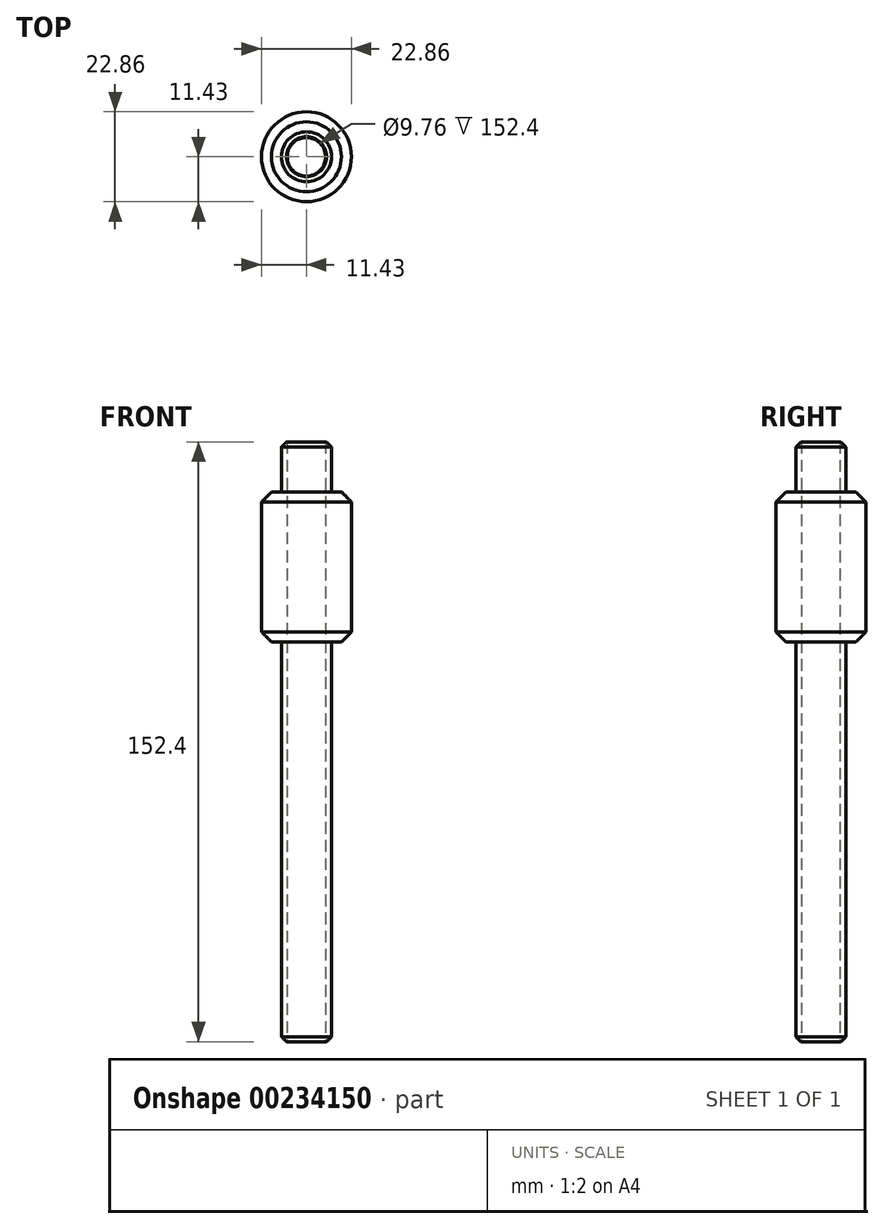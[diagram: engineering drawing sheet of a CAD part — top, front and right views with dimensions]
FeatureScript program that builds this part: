
annotation { "Feature Type Name" : "Feature", "Feature Type Description" : "" }
export const myFeature = defineFeature(function(context is Context, id is Id, definition is map)
    precondition{}
    {
        {
            var Q0;
            Q0=qCreatedBy(makeId("Front.planeOp"),FACE);
            var sketch = newSketch(context, id + "F0", { "sketchPlane" : qUnion([Q0])});
            skLineSegment(sketch, "E0.bottom", {"start": v(6.35, -76.2) * mm, "end": v(-6.35, -76.2) * mm});
            skLineSegment(sketch, "E0.top", {"start": v(6.35, 76.2) * mm, "end": v(-6.35, 76.2) * mm});
            skLineSegment(sketch, "E0.left", {"start": v(6.35, -76.2) * mm, "end": v(6.35, 25.4) * mm});
            skLineSegment(sketch, "E0.right", {"start": v(-6.35, -76.2) * mm, "end": v(-6.35, 76.2) * mm});
            skPoint(sketch, "E0.middle", {"position": v(0, 0) * mm});
            skLineSegment(sketch, "E1", {"start": v(6.35, 63.5) * mm, "end": v(11.43, 63.5) * mm});
            skLineSegment(sketch, "E2", {"start": v(11.43, 63.5) * mm, "end": v(11.43, 25.4) * mm});
            skLineSegment(sketch, "E3", {"start": v(11.43, 25.4) * mm, "end": v(6.35, 25.4) * mm});
            skLineSegment(sketch, "E4.trimOffspring", {"start": v(6.35, 63.5) * mm, "end": v(6.35, 76.2) * mm});
            skLineSegment(sketch, "E5", {"start": v(0, 89.32) * mm, "end": v(0, -93.51) * mm});
            skPoint(sketch, "E5.startSnap0", {"position": v(0, 76.2) * mm});
            skSolve(sketch);
        }
        {
            var Q0;
            {var subQ0=sQuery(id+"F0.wireOp",EDGE,"E0.left");Q0=makeQuery(id+"F0.imprint","IMPRINT",FACE,{"disambiguationData":[TD([[makeQuery(id+"F0.imprint","IMPRINT",EDGE,{"derivedFrom":subQ0}),1.0]])]});}
            var Q1;
            Q1=sQuery(id+"F0.wireOp",EDGE,"E5");
            revolve(context, id + "F1", {"entities" : qUnion([Q0]), "axis" : qUnion([Q1]), "revolveType" : RevolveType.FULL});
        }
        {
            var Q0;
            Q0=makeQuery(id+"F1.opRevolve","SWEPT_EDGE",EDGE,{"disambiguationData":[OSD([sQuery(id+"F0.wireOp",EDGE,"E2"),sQuery(id+"F0.wireOp",EDGE,"E3")])]});
            chamfer(context, id + "F2", {"entities" : qUnion([Q0]), "width" : 2.54 * mm, "tangentPropagation" : true});
        }
        {
            var Q0;
            Q0=makeQuery(id+"F1.opRevolve","SWEPT_FACE",FACE,{"disambiguationData":[OSD([sQuery(id+"F0.wireOp",EDGE,"E0.bottom")])]});
            var sketch = newSketch(context, id + "F3", { "sketchPlane" : qUnion([Q0])});
            skCircle(sketch, "E6", {"center": v(0, 0) * mm, "radius": 4.88 * mm});
            skSolve(sketch);
        }
        {
            var Q0;
            Q0=makeQuery(id+"F3.imprint","IMPRINT",FACE,{"disambiguationData":[TD([[makeQuery(id+"F3.imprint","IMPRINT",EDGE,{"derivedFrom":sQuery(id+"F3.wireOp",EDGE,"E6")}),1.0]])]});
            extrude(context, id + "F6", {"entities" : qUnion([Q0]), "operationType" : NewBodyOperationType.REMOVE, "endBound" : BoundingType.THROUGH_ALL, "oppositeDirection" : true, "depth" : 25.4 * mm});
        }
        {
            var Q0;
            Q0=makeQuery(id+"F1.opRevolve","SWEPT_EDGE",EDGE,{"disambiguationData":[OSD([sQuery(id+"F0.wireOp",EDGE,"E0.top"),sQuery(id+"F0.wireOp",EDGE,"E4.trimOffspring")])]});
            chamfer(context, id + "F4", {"entities" : qUnion([Q0]), "width" : 1.27 * mm, "tangentPropagation" : true});
        }
        {
            var Q0;
            Q0=makeQuery(id+"F1.opRevolve","SWEPT_EDGE",EDGE,{"disambiguationData":[OSD([sQuery(id+"F0.wireOp",EDGE,"E1"),sQuery(id+"F0.wireOp",EDGE,"E2")])]});
            chamfer(context, id + "F7", {"entities" : qUnion([Q0]), "width" : 2.54 * mm, "tangentPropagation" : true});
        }
        {
            var Q0;
            Q0=makeQuery(id+"F1.opRevolve","SWEPT_EDGE",EDGE,{"disambiguationData":[OSD([sQuery(id+"F0.wireOp",EDGE,"E0.bottom"),sQuery(id+"F0.wireOp",EDGE,"E0.left")])]});
            chamfer(context, id + "F5", {"entities" : qUnion([Q0]), "width" : 1.27 * mm, "tangentPropagation" : true});
        }
    });
